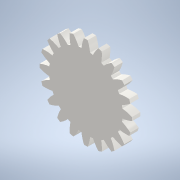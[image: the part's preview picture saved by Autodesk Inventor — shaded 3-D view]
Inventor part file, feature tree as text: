
AUTODESK INVENTOR PART (.ipt)
format: ipt  version: 2021 (Build 250183000, 183)  size: 218,624 bytes
history: native  units: mm (DEFAULTED — no unit token found)
features: plane x3, other x3, sketch x2, extrude x1
ambient origin geometry x8: Origin, YZ Plane, XZ Plane, XY Plane, X Axis, Y Axis, Z Axis, Center Point
bodies: Solid1 (feature_tree)
feature tree (9):
  extrude  "Extrusion1"  Depth=20.0mm TaperAngle=0.0deg
  plane  "Work Plane2"
  plane  "Work Plane8"
  plane  "Work Plane9"
  other  "Engrenage cylindrique"
  sketch  "Sketch1"  dims[d0=77.0mm d1=20.0mm d2=0.0mm]
  sketch  "Sketch2"  dims[d3=70.0mm d4=50.0mm d5=0.0mm d16=63.0mm d17=0.0mm d34=1.570796mm d39=0.0mm d41=0.0mm d43=63.0mm d46=63.0mm d47=0.0mm d48=0.0mm]
  other  "Srf1"
  other  "Diamètre primitif"
